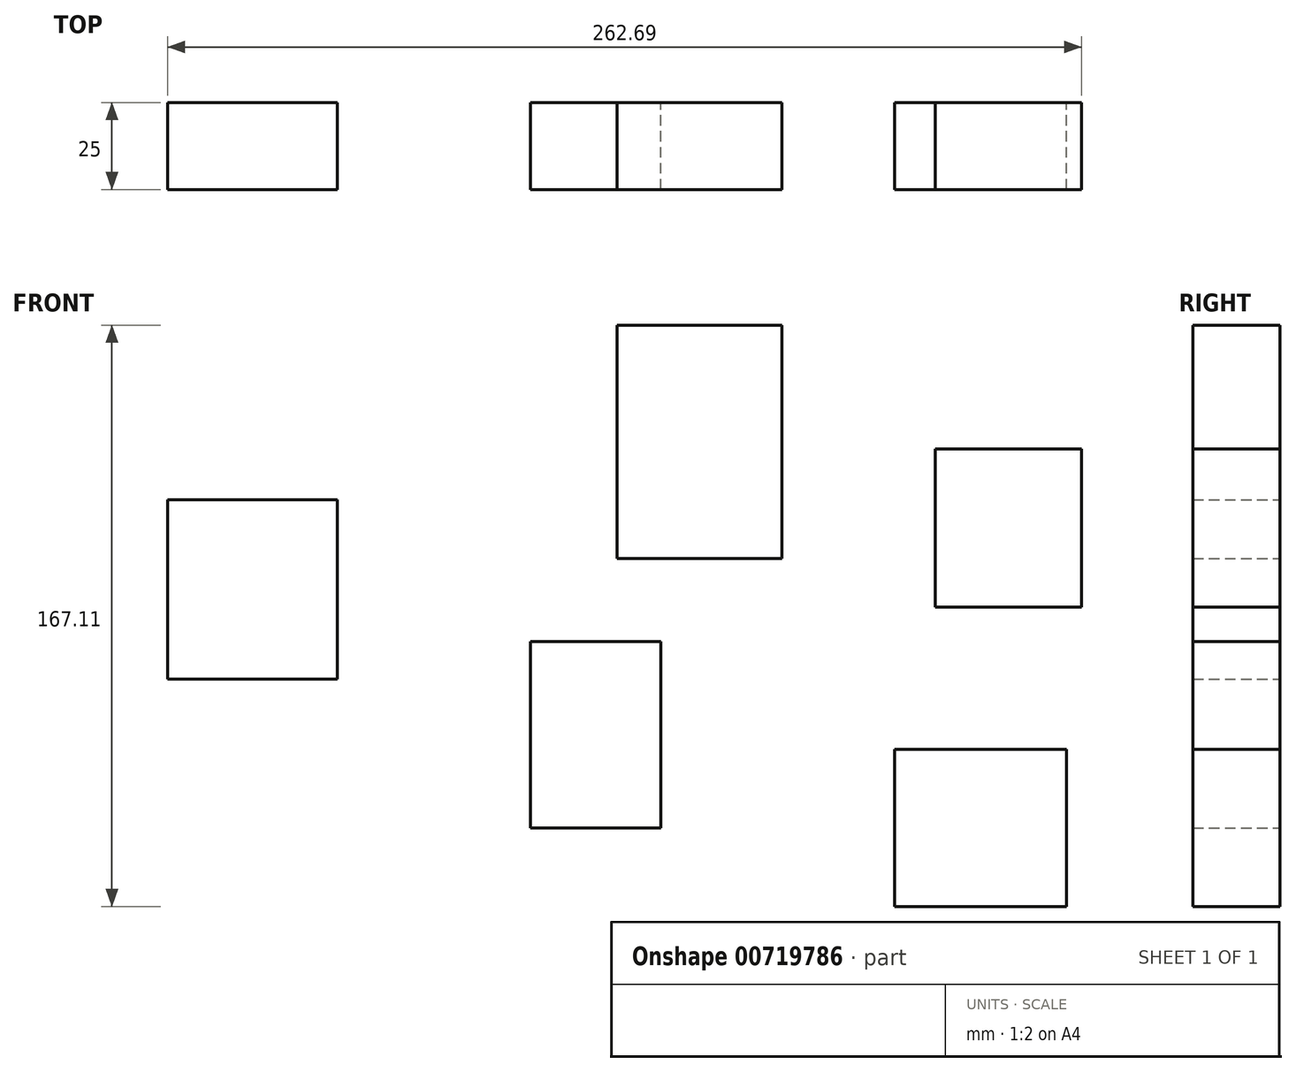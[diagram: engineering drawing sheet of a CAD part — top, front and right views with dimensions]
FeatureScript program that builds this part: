
annotation { "Feature Type Name" : "Feature", "Feature Type Description" : "" }
export const myFeature = defineFeature(function(context is Context, id is Id, definition is map)
    precondition{}
    {
        {
            var Q0;
            Q0=qCreatedBy(makeId("Front.planeOp"),FACE);
            var sketch = newSketch(context, id + "F0", { "sketchPlane" : qUnion([Q0])});
            skLineSegment(sketch, "E0.bottom", {"start": v(-123, 16.06) * mm, "end": v(-74.27, 16.06) * mm});
            skLineSegment(sketch, "E0.top", {"start": v(-123, 67.52) * mm, "end": v(-74.27, 67.52) * mm});
            skLineSegment(sketch, "E0.left", {"start": v(-123, 16.06) * mm, "end": v(-123, 67.52) * mm});
            skLineSegment(sketch, "E0.right", {"start": v(-74.27, 16.06) * mm, "end": v(-74.27, 67.52) * mm});
            skPoint(sketch, "E0.middle", {"position": v(-98.63, 41.79) * mm});
            skLineSegment(sketch, "E1.bottom", {"start": v(-18.7, -26.76) * mm, "end": v(18.7, -26.76) * mm});
            skLineSegment(sketch, "E1.top", {"start": v(-18.7, 26.76) * mm, "end": v(18.7, 26.76) * mm});
            skLineSegment(sketch, "E1.left", {"start": v(-18.7, -26.76) * mm, "end": v(-18.7, 26.76) * mm});
            skLineSegment(sketch, "E1.right", {"start": v(18.7, -26.76) * mm, "end": v(18.7, 26.76) * mm});
            skPoint(sketch, "E1.middle", {"position": v(0, 0) * mm});
            skLineSegment(sketch, "E2.bottom", {"start": v(6.18, 50.68) * mm, "end": v(53.57, 50.68) * mm});
            skLineSegment(sketch, "E2.top", {"start": v(6.18, 117.77) * mm, "end": v(53.57, 117.77) * mm});
            skLineSegment(sketch, "E2.left", {"start": v(6.18, 50.68) * mm, "end": v(6.18, 117.77) * mm});
            skLineSegment(sketch, "E2.right", {"start": v(53.57, 50.68) * mm, "end": v(53.57, 117.77) * mm});
            skPoint(sketch, "E2.middle", {"position": v(29.87, 84.23) * mm});
            skLineSegment(sketch, "E3.bottom", {"start": v(97.63, 36.7) * mm, "end": v(139.69, 36.7) * mm});
            skLineSegment(sketch, "E3.top", {"start": v(97.63, 82.22) * mm, "end": v(139.69, 82.22) * mm});
            skLineSegment(sketch, "E3.left", {"start": v(97.63, 36.7) * mm, "end": v(97.63, 82.22) * mm});
            skLineSegment(sketch, "E3.right", {"start": v(139.69, 36.7) * mm, "end": v(139.69, 82.22) * mm});
            skPoint(sketch, "E3.middle", {"position": v(118.66, 59.46) * mm});
            skLineSegment(sketch, "E4.bottom", {"start": v(85.95, -49.34) * mm, "end": v(135.35, -49.34) * mm});
            skLineSegment(sketch, "E4.top", {"start": v(85.95, -4.17) * mm, "end": v(135.35, -4.17) * mm});
            skLineSegment(sketch, "E4.left", {"start": v(85.95, -49.34) * mm, "end": v(85.95, -4.17) * mm});
            skLineSegment(sketch, "E4.right", {"start": v(135.35, -49.34) * mm, "end": v(135.35, -4.17) * mm});
            skPoint(sketch, "E4.middle", {"position": v(110.65, -26.76) * mm});
            skSolve(sketch);
        }
        {
            var Q0;
            Q0=makeQuery(id+"F0.imprint","IMPRINT",FACE,{"disambiguationData":[TD([[makeQuery(id+"F0.imprint","IMPRINT",EDGE,{"derivedFrom":sQuery(id+"F0.wireOp",EDGE,"E1.bottom")}),1.0]])]});
            var Q1;
            Q1=makeQuery(id+"F0.imprint","IMPRINT",FACE,{"disambiguationData":[TD([[makeQuery(id+"F0.imprint","IMPRINT",EDGE,{"derivedFrom":sQuery(id+"F0.wireOp",EDGE,"E2.bottom")}),1.0]])]});
            var Q2;
            Q2=makeQuery(id+"F0.imprint","IMPRINT",FACE,{"disambiguationData":[TD([[makeQuery(id+"F0.imprint","IMPRINT",EDGE,{"derivedFrom":sQuery(id+"F0.wireOp",EDGE,"E3.bottom")}),1.0]])]});
            var Q3;
            Q3=makeQuery(id+"F0.imprint","IMPRINT",FACE,{"disambiguationData":[TD([[makeQuery(id+"F0.imprint","IMPRINT",EDGE,{"derivedFrom":sQuery(id+"F0.wireOp",EDGE,"E4.bottom")}),1.0]])]});
            var Q4;
            Q4=makeQuery(id+"F0.imprint","IMPRINT",FACE,{"disambiguationData":[TD([[makeQuery(id+"F0.imprint","IMPRINT",EDGE,{"derivedFrom":sQuery(id+"F0.wireOp",EDGE,"E0.bottom")}),1.0]])]});
            extrude(context, id + "F1", {"entities" : qUnion([Q0, Q1, Q2, Q3, Q4]), "depth" : 25 * mm, "offsetDistance" : 25 * mm});
        }
    });
